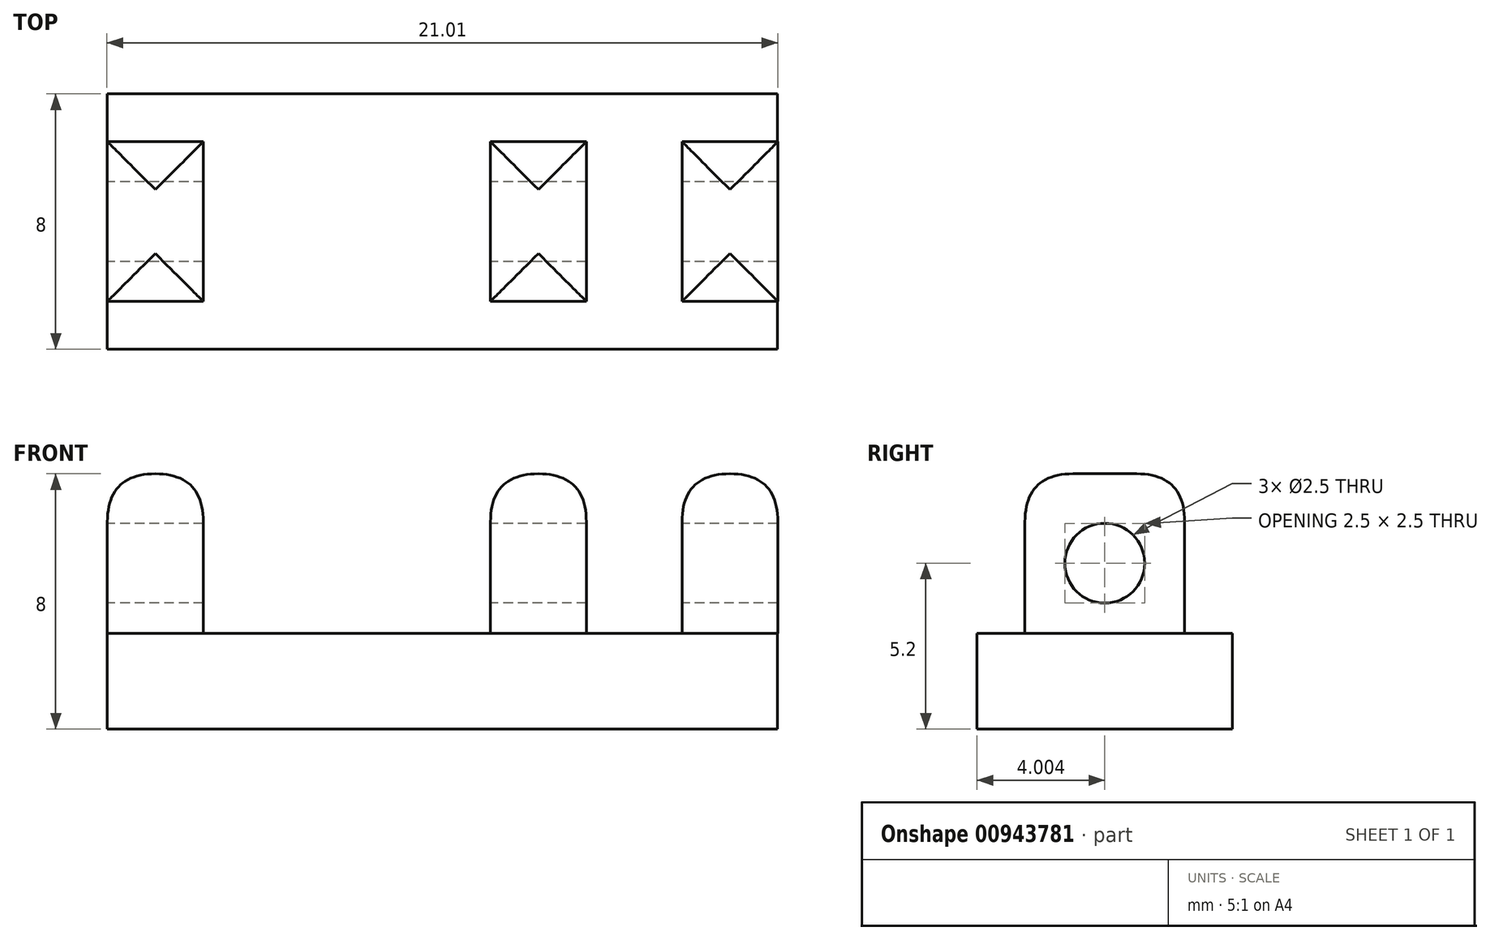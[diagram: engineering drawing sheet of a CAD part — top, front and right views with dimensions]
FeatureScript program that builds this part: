
annotation { "Feature Type Name" : "Feature", "Feature Type Description" : "" }
export const myFeature = defineFeature(function(context is Context, id is Id, definition is map)
    precondition{}
    {
        {
            var Q0;
            Q0=qCreatedBy(makeId("Top.planeOp"),FACE);
            var sketch = newSketch(context, id + "F0", { "sketchPlane" : qUnion([Q0])});
            skLineSegment(sketch, "E0.bottom", {"start": v(-69.72, 54.78) * mm, "end": v(-48.72, 54.78) * mm});
            skLineSegment(sketch, "E0.top", {"start": v(-69.72, 46.78) * mm, "end": v(-48.72, 46.78) * mm});
            skLineSegment(sketch, "E0.right", {"start": v(-48.72, 54.78) * mm, "end": v(-48.72, 46.78) * mm});
            skLineSegment(sketch, "E1.MirrorCS", {"start": v(-54.7, 48.28) * mm, "end": v(-57.7, 48.28) * mm});
            skLineSegment(sketch, "E2.MirrorCS", {"start": v(-54.7, 53.28) * mm, "end": v(-54.7, 48.28) * mm});
            skLineSegment(sketch, "E3.MirrorCS", {"start": v(-54.7, 53.28) * mm, "end": v(-57.7, 53.28) * mm});
            skLineSegment(sketch, "E4", {"start": v(-57.7, 53.28) * mm, "end": v(-57.7, 48.28) * mm});
            skPoint(sketch, "E5", {"position": v(-59.2, 50.78) * mm});
            skLineSegment(sketch, "E6", {"start": v(-69.72, 54.78) * mm, "end": v(-69.72, 46.78) * mm});
            skPoint(sketch, "E7", {"position": v(-56.2, 48.28) * mm});
            skSolve(sketch);
        }
        {
            var Q0;
            Q0=makeQuery(id+"F0.imprint","IMPRINT",FACE,{"disambiguationData":[TD([[makeQuery(id+"F0.imprint","IMPRINT",EDGE,{"derivedFrom":sQuery(id+"F0.wireOp",EDGE,"E1.MirrorCS")}),-1.0]])]});
            extrude(context, id + "F1", {"entities" : qUnion([Q0]), "depth" : 5 * mm, "offsetDistance" : 25 * mm});
        }
        {
            var Q0;
            Q0=makeQuery(id+"F1.opExtrude","CAP_EDGE",EDGE,{"disambiguationData":[OSD([sQuery(id+"F0.wireOp",EDGE,"E2.MirrorCS")])],"isStart":false});
            var Q1;
            Q1=makeQuery(id+"F1.opExtrude","CAP_EDGE",EDGE,{"disambiguationData":[OSD([sQuery(id+"F0.wireOp",EDGE,"E4")])],"isStart":false});
            var Q2;
            Q2=makeQuery(id+"F1.opExtrude","CAP_EDGE",EDGE,{"disambiguationData":[OSD([sQuery(id+"F0.wireOp",EDGE,"E3.MirrorCS")])],"isStart":false});
            var Q3;
            Q3=makeQuery(id+"F1.opExtrude","CAP_EDGE",EDGE,{"disambiguationData":[OSD([sQuery(id+"F0.wireOp",EDGE,"E1.MirrorCS")])],"isStart":false});
            fillet(context, id + "F2", {"entities" : qUnion([Q0, Q1, Q2, Q3]), "radius" : 1.5 * mm, "rho" : 0.5, "crossSection" : FilletCrossSection.CONIC, "allowEdgeOverflow" : false});
        }
        {
            var Q0;
            Q0=makeQuery(id+"F1.opExtrude","SWEPT_FACE",FACE,{"disambiguationData":[OSD([sQuery(id+"F0.wireOp",EDGE,"E4")])]});
            var sketch = newSketch(context, id + "F3", { "sketchPlane" : qUnion([Q0])});
            skCircle(sketch, "E8", {"center": v(-50.78, 2.2) * mm, "radius": 1.25 * mm});
            skPoint(sketch, "E8.centerSnap0", {"position": v(-50.78, 0) * mm});
            skPoint(sketch, "E8.centerSnap1", {"position": v(-48.28, 1.75) * mm});
            skSolve(sketch);
        }
        {
            var Q0;
            Q0=makeQuery(id+"F3.imprint","IMPRINT",FACE,{"disambiguationData":[TD([[makeQuery(id+"F3.imprint","IMPRINT",EDGE,{"derivedFrom":sQuery(id+"F3.wireOp",EDGE,"E8")}),1.0]])]});
            extrude(context, id + "F4", {"entities" : qUnion([Q0]), "operationType" : NewBodyOperationType.REMOVE, "oppositeDirection" : true, "depth" : 3.03 * mm, "offsetDistance" : 25 * mm});
        }
        {
            var Q0;
            Q0=makeQuery(id+"F1.opExtrude","SWEPT_BODY",BODY,{"disambiguationData":[OSD([sQuery(id+"F0.wireOp",EDGE,"E1.MirrorCS"),sQuery(id+"F0.wireOp",EDGE,"E2.MirrorCS"),sQuery(id+"F0.wireOp",EDGE,"E3.MirrorCS"),sQuery(id+"F0.wireOp",EDGE,"E4")])]});
            transform(context, id + "F5", {"entities" : qUnion([Q0]), "transformType" : TransformType.TRANSLATION_3D, "dx" : 6 * mm, "dy" : 0 * mm, "dz" : 0 * mm, "makeCopy" : true});
        }
        {
            var Q0;
            Q0=makeQuery(id+"F5.opPattern","COPY",BODY,{"derivedFrom":makeQuery(id+"F1.opExtrude","SWEPT_BODY",BODY,{"disambiguationData":[OSD([sQuery(id+"F0.wireOp",EDGE,"E1.MirrorCS"),sQuery(id+"F0.wireOp",EDGE,"E2.MirrorCS"),sQuery(id+"F0.wireOp",EDGE,"E3.MirrorCS"),sQuery(id+"F0.wireOp",EDGE,"E4")])]}),"instanceName":"1"});
            transform(context, id + "F6", {"entities" : qUnion([Q0]), "transformType" : TransformType.TRANSLATION_3D, "dx" : -3 * mm, "dy" : 0 * mm, "dz" : 0 * mm, "makeCopy" : true});
        }
        {
            var Q0;
            Q0=makeQuery(id+"F6.opPattern","COPY",BODY,{"derivedFrom":makeQuery(id+"F5.opPattern","COPY",BODY,{"derivedFrom":makeQuery(id+"F1.opExtrude","SWEPT_BODY",BODY,{"disambiguationData":[OSD([sQuery(id+"F0.wireOp",EDGE,"E1.MirrorCS"),sQuery(id+"F0.wireOp",EDGE,"E2.MirrorCS"),sQuery(id+"F0.wireOp",EDGE,"E3.MirrorCS"),sQuery(id+"F0.wireOp",EDGE,"E4")])]}),"instanceName":"1"}),"instanceName":"1"});
            transform(context, id + "F7", {"entities" : qUnion([Q0]), "transformType" : TransformType.TRANSLATION_3D, "dx" : -15 * mm, "dy" : 0 * mm, "dz" : 0 * mm, "makeCopy" : false});
        }
        {
            var Q0;
            Q0=makeQuery(id+"F1.opExtrude","SWEPT_BODY",BODY,{"disambiguationData":[OSD([sQuery(id+"F0.wireOp",EDGE,"E1.MirrorCS"),sQuery(id+"F0.wireOp",EDGE,"E2.MirrorCS"),sQuery(id+"F0.wireOp",EDGE,"E3.MirrorCS"),sQuery(id+"F0.wireOp",EDGE,"E4")])]});
            var Q1;
            Q1=makeQuery(id+"F5.opPattern","COPY",BODY,{"derivedFrom":makeQuery(id+"F1.opExtrude","SWEPT_BODY",BODY,{"disambiguationData":[OSD([sQuery(id+"F0.wireOp",EDGE,"E1.MirrorCS"),sQuery(id+"F0.wireOp",EDGE,"E2.MirrorCS"),sQuery(id+"F0.wireOp",EDGE,"E3.MirrorCS"),sQuery(id+"F0.wireOp",EDGE,"E4")])]}),"instanceName":"1"});
            var Q2;
            Q2=makeQuery(id+"F6.opPattern","COPY",BODY,{"derivedFrom":makeQuery(id+"F5.opPattern","COPY",BODY,{"derivedFrom":makeQuery(id+"F1.opExtrude","SWEPT_BODY",BODY,{"disambiguationData":[OSD([sQuery(id+"F0.wireOp",EDGE,"E1.MirrorCS"),sQuery(id+"F0.wireOp",EDGE,"E2.MirrorCS"),sQuery(id+"F0.wireOp",EDGE,"E3.MirrorCS"),sQuery(id+"F0.wireOp",EDGE,"E4")])]}),"instanceName":"1"}),"instanceName":"1"});
            transform(context, id + "F8", {"entities" : qUnion([Q0, Q1, Q2]), "transformType" : TransformType.TRANSLATION_3D, "dx" : 0 * mm, "dy" : 0 * mm, "dz" : 3 * mm, "makeCopy" : false});
        }
        {
            var Q0;
            Q0=makeQuery(id+"F0.imprint","IMPRINT",FACE,{"disambiguationData":[TD([[makeQuery(id+"F0.imprint","IMPRINT",EDGE,{"derivedFrom":sQuery(id+"F0.wireOp",EDGE,"E0.bottom")}),-1.0]])]});
            var Q1;
            Q1=makeQuery(id+"F0.imprint","IMPRINT",FACE,{"disambiguationData":[TD([[makeQuery(id+"F0.imprint","IMPRINT",EDGE,{"derivedFrom":sQuery(id+"F0.wireOp",EDGE,"E1.MirrorCS")}),-1.0]])]});
            extrude(context, id + "F9", {"entities" : qUnion([Q0, Q1]), "depth" : 3 * mm, "offsetDistance" : 25 * mm});
        }
    });
